# Revit family: Gira_222500
name_source: partatom
category: Elektroinstallationen
revit_build: Autodesk Revit 2017 (Build: 20160225_1515(x64)
units: mm (PartAtom-declared; Revit-internal decimal feet)

## family parameters
Basisbauteil = Fläche
Beim Laden mit Abzugskörper schneiden = Nein
Bemaßung runder Anschluss = Durchmesser verwenden
Beschriftungsausrichtung beibehalten = Nein
Gemeinsam genutzt = Nein
Raumberechnungspunkt = Nein
Teiletyp = Normal

## types (1)
- Gira_222500
    Andere Bussysteme = ohne
    Ausführung = Präsenzmelder
    Ausführung der Oberfläche = nicht zutreffend
    BIM = https://media.stage.bim.site
    Beschreibung = KNX Präsenzmelder Mini Komfort   Präsenzmelder zur Anwesenheitsüberwachung (Betriebsart: Präsenzmelder), zur Bewegungserkennung (Betriebsart: Deckenwächter) oder zur Überwachung durch Meldetelegramme (Betriebsart: Melder) in Innenräumen oder Außenbereichen. Durch das dezente Design, die besonders flache Bauweise und das flexible Montagekonzept eignen sich die Präsenzmelder Mini gut für Objekte mit hohem architektonischen Anspruch.  Merkmale: - Extrem flacher Einbau. - Klemmmontage an abgehangenen Decken. - Deckenmontage an festen Decken in Gerätedose nach DIN 49073 mittels optionalem Zubehör. - Aufputz-Montage in Aufputz-Gerätedose (optionales Zubehör). - Schutzart IP44 ermöglicht Montage im Außenbereich bzw. in Feuchträumen. - Mit Farbe überstreichbarer Designring ermöglicht die farbliche Anpassung an die Wand oder die Decke. - Nach Entfernen des Designrings sind alle Bedienelemente (z. B. Programmier-Taste) des Geräts bequem von vorne erreichbar. Dadurch ist kein Ausbau bei nachträglicher Justierung oder Programmierung über die ETS notwendig. - Deckeneinbaugerät mit integrierter KNX Busankopplung. - PIR-Sensorik: drei Sensoren, integrierter Helligkeitssensor. - Empfindlichkeit der Bewegungserfassung über Einsteller manuell einstellbar. - Empfindlichkeit über ETS konfigurierbar. - Empfindlichkeitseinsteller am Gerät über Software deaktivierbar. - Anzeige der Bewegungserfassung (permanent oder nur im Gehtest). - Separate Auswertung im Fernbereich der drei PIR-Sensoren mit je 120 Erfassungsbereich mit Überlappung. - Handbetätigung durch IR-Fernbedienung. - Maximal 5 + 2 Funktionsblöcke konfigurierbar. - Funktionsblöcke 1 bis 5 jeweils einstellbare Funktion: Deckenwächter, Präsenzmelder, Meldebetrieb. - Funktionsblock 6: Präsenzmelder mit Lichtregelung. - Funktionsblock 7: Helligkeitssensor mit Grenzwertüberwachung. - Funktionsblock-Umschaltung z. B. für Tag- Nachbetrieb oder Wochen- Wochenendbetrieb. - Funktionsblöcke 1 bis 5: Einzelgerät, Hauptstelle, Nebenstelle einstellbar. - Einstellbare Betriebsart bei Einzelgerät als Hauptstelle: Automatik, Halbautomatik (Manuell EIN   Automatik AUS bzw. Automatik EIN   Manuell AUS). - Zwei Ausgänge pro Funktionsblock (1 bis 5) bei Funktion Deckenwächter, Präsenzmelder. - Funktionen Deckenwächter, Präsenzmelder pro Ausgang: Schalten, Treppenhausfunktion, Schalten mit Zwangsstellung, Dimmwertgeber, Lichtszenennebenstelle, Temperaturwertgeber, Helligkeitswertgeber, Temperatur-Betriebsmodus. - Deckenwächter, Präsenzmelder: Dämmerungsstufe einstellbar, Dämmerungsstufe über externes Kommunikationsobjekt oder per Teach-in, zusätzliche Sendeverzögerung über externes Kommunikationsobjekt, adaptive Nachlaufzeit (Selbstlernende zusätzliche Sendeverzögerung), Kurzzeit-Präsenzfunktion, Rückmeldung der Dämmerungsstufe, Sperrfunktion, manuelle Bedienung über Tastsensor (separates Kommunikationsobjekt), Abschalthelligkeit (bei Präsenzmelder) über Teach-In, Messung der Zeitspanne nach letzter Bewegung. - Funktion Präsenzmelder mit Lichtregelung: Kombination mit Funktionsblock Präsenzmelder oder Einzelgerät, Sollwert einstellbar, Sollwertvorgabe über externes Kommunikationsobjekt, Sollwertverschiebung über externes Kommunikationsobjekt, Teach-In Funktion, Rückmeldung des effektiven Sollwertes. - Funktion Helligkeitssensor mit Grenzwertüberwachung: bis zu drei Grenzwerte konfigurierbar, Funktionen Schalten, Dimmwertgeber, Lichtszenennebenstelle, Hysterese konfigurierbar, Grenzwert über externes Kommunikationsobjekt oder Teach-In, Sperrfunktion.  Hinweise : - Der Präsenzmelder Mini ist nicht für Alarmmeldungen in VdS-konformen Alarmanlagen geeignet.
    Bussystem Funkbus = Nein
    Bussystem KNX = Ja
    Bussystem KNX-Funk = Nein
    Bussystem LON = Nein
    Bussystem Powernet = Nein
    Datenblatt = https://katalog.gira.de
    Farbe = weiß
    GTIN = 4010337014690
    HAN = 222500
    Hersteller = Gira
    Montageart = Aufputz
    Oberfläche = sonstige
    Produktseite = http://katalog.gira.de
    Transparent = Nein
    Typname = Präsenzm. Mini Komfort KNX
    URL = https://www.gira.de
    Vorgabe-Ansicht = 1219 mm
    Werkstoff = sonstige
    Werkstoffgüte = sonstige

## geometry (parser evidence)
native form markers: Sweep x3
no freeform markers — native parametric forms only
